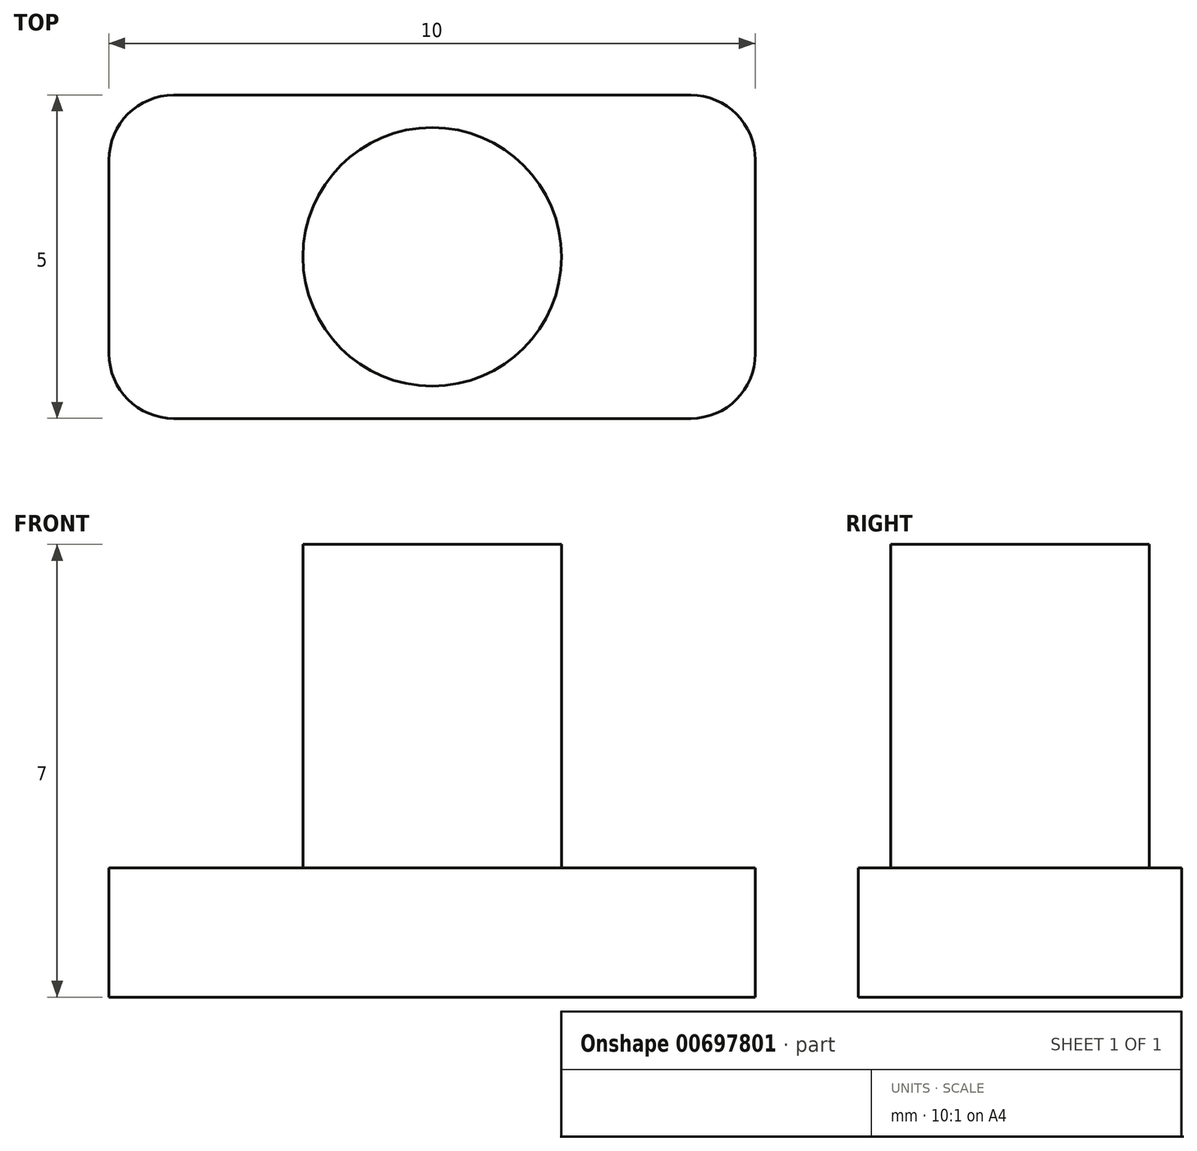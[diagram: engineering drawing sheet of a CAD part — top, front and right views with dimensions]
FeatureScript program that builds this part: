
annotation { "Feature Type Name" : "Feature", "Feature Type Description" : "" }
export const myFeature = defineFeature(function(context is Context, id is Id, definition is map)
    precondition{}
    {
        {
            var Q0;
            Q0=qCreatedBy(makeId("Top.planeOp"),FACE);
            var sketch = newSketch(context, id + "F0", { "sketchPlane" : qUnion([Q0])});
            skLineSegment(sketch, "E0.bottom", {"start": v(-7.32, -6.03) * mm, "end": v(0.68, -6.03) * mm});
            skLineSegment(sketch, "E0.top", {"start": v(-7.32, -11.03) * mm, "end": v(0.68, -11.03) * mm});
            skLineSegment(sketch, "E0.left", {"start": v(-8.32, -7.03) * mm, "end": v(-8.32, -10.03) * mm});
            skLineSegment(sketch, "E0.right", {"start": v(1.68, -7.03) * mm, "end": v(1.68, -10.03) * mm});
            skPoint(sketch, "E1.visualSharp", {"position": v(-8.32, -6.03) * mm});
            skArc(sketch, "E1.filletArc", {"start": v(-7.32, -6.03) * mm, "mid": v(-8.02, -6.33) * mm, "end": v(-8.32, -7.03) * mm});
            skPoint(sketch, "E2.visualSharp", {"position": v(1.68, -6.03) * mm});
            skArc(sketch, "E2.filletArc", {"start": v(1.68, -7.03) * mm, "mid": v(1.4, -6.33) * mm, "end": v(0.68, -6.03) * mm});
            skPoint(sketch, "E3.visualSharp", {"position": v(1.68, -11.03) * mm});
            skArc(sketch, "E3.filletArc", {"start": v(0.68, -11.03) * mm, "mid": v(1.4, -10.74) * mm, "end": v(1.68, -10.03) * mm});
            skPoint(sketch, "E4.visualSharp", {"position": v(-8.32, -11.03) * mm});
            skArc(sketch, "E4.filletArc", {"start": v(-8.32, -10.03) * mm, "mid": v(-8.02, -10.74) * mm, "end": v(-7.32, -11.03) * mm});
            skSolve(sketch);
        }
        {
            var Q0;
            Q0=makeQuery(id+"F0.imprint","IMPRINT",FACE,{"disambiguationData":[TD([[makeQuery(id+"F0.imprint","IMPRINT",EDGE,{"derivedFrom":sQuery(id+"F0.wireOp",EDGE,"E0.bottom")}),-1.0]])]});
            extrude(context, id + "F1", {"entities" : qUnion([Q0]), "depth" : 2 * mm, "offsetDistance" : 25 * mm});
        }
        {
            var Q0;
            Q0=makeQuery(id+"F1.opExtrude","CAP_FACE",FACE,{"disambiguationData":[OSD([sQuery(id+"F0.wireOp",EDGE,"E0.bottom"),sQuery(id+"F0.wireOp",EDGE,"E0.top"),sQuery(id+"F0.wireOp",EDGE,"E0.left"),sQuery(id+"F0.wireOp",EDGE,"E0.right"),sQuery(id+"F0.wireOp",EDGE,"E1.filletArc"),sQuery(id+"F0.wireOp",EDGE,"E2.filletArc"),sQuery(id+"F0.wireOp",EDGE,"E3.filletArc"),sQuery(id+"F0.wireOp",EDGE,"E4.filletArc")])],"isStart":false});
            var sketch = newSketch(context, id + "F2", { "sketchPlane" : qUnion([Q0])});
            skCircle(sketch, "E5", {"center": v(-3.32, -8.53) * mm, "radius": 2 * mm});
            skSolve(sketch);
        }
        {
            var Q0;
            Q0=makeQuery(id+"F2.imprint","IMPRINT",FACE,{"disambiguationData":[TD([[makeQuery(id+"F2.imprint","IMPRINT",EDGE,{"derivedFrom":sQuery(id+"F2.wireOp",EDGE,"E5")}),1.0]])]});
            extrude(context, id + "F3", {"entities" : qUnion([Q0]), "operationType" : NewBodyOperationType.ADD, "depth" : 5 * mm, "offsetDistance" : 25 * mm});
        }
    });
